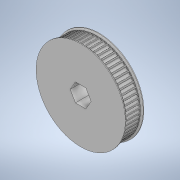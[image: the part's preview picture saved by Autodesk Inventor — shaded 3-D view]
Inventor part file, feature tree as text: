
AUTODESK INVENTOR PART (.ipt)
format: ipt  version: 2022.3 (Build 263350000, 350)  size: 524,800 bytes
history: native  units: in
note: dims shown in document units (in); Inventor stores cm internally (conversion verified against a paired STEP export)
features: extrude x7, sketch x7, fillet x2, pattern_circular x2, mirror x2, chamfer x2, other x1
ambient origin geometry x8: Origin, YZ Plane, XZ Plane, XY Plane, X Axis, Y Axis, Z Axis, Center Point
bodies: Solid1 (feature_tree)
feature tree (23):
  other  "Hex Bore"
  extrude  "HTD Base"  Depth=0.3937in TaperAngle=0.0deg
  extrude  "HTD Base Tooth"  Depth=0.0113in
  fillet  "HTD Base Tooth pt. 2"  [1 undecoded]
  pattern_circular  "HTD Teeth"  Count=64  [1 undecoded]
  extrude  "HTD Flange"  Depth=0.0394in
  mirror  "HTD Flanges"
  chamfer  "HTD Flange Chamfer"  Distance=0.0787in Angle=45.0deg
  extrude  "GT2 Base"  Depth=0.5in
  extrude  "GT2 Base Tooth"  TaperAngle=0.0deg  [1 undecoded]
  fillet  "GT2 Base Tooth pt. 2"  Radius=0.5in
  pattern_circular  "GT2 Teeth"  [2 undecoded]
  extrude  "GT2 Flange"  Depth=0.0591in
  mirror  "GT2 Flanges"
  chamfer  "GT2 Flange Chamfer"  Distance=0.3937in
  extrude  "Circle Bore"  TaperAngle=0.0deg  [1 undecoded]
  sketch  "Sketch1"  dims[d0=3.9652in d1=0.3937in d2=0.0in]
  sketch  "Sketch2"  dims[d3=0.1208in d5=0.0113in d6=0.0in d7=0.0in]
  sketch  "Sketch3"  dims[d8=0.0169in d9=25.1969in]
  sketch  "Sketch4"  dims[d10=360.0deg d12=0.0394in]
  sketch  "Sketch5"  dims[d13=0.0591in]
  sketch  "Sketch6"  dims[d14=0.0in]
  sketch  "Sketch7"  dims[d15=0.0394in d16=0.0787in d17=45.0deg d18=0.5in d19=0.0in d20=0.0in d21=0.5in d22=0.0in d23=0.0in d24=2.3761in d25=0.3937in d26=0.0in d27=0.0727in d28=0.0075in d29=0.0in d30=0.0in d31=0.0118in d32=25.1969in d33=360.0deg d35=0.0394in d36=0.0591in d37=0.0in d38=0.0394in d39=0.0787in d40=45.0deg]
note: 6 required parameter values undecoded (feature->parameter linkage not recoverable at this tier; creation-order binding heuristic only, values carry confidence <= 0.55)
